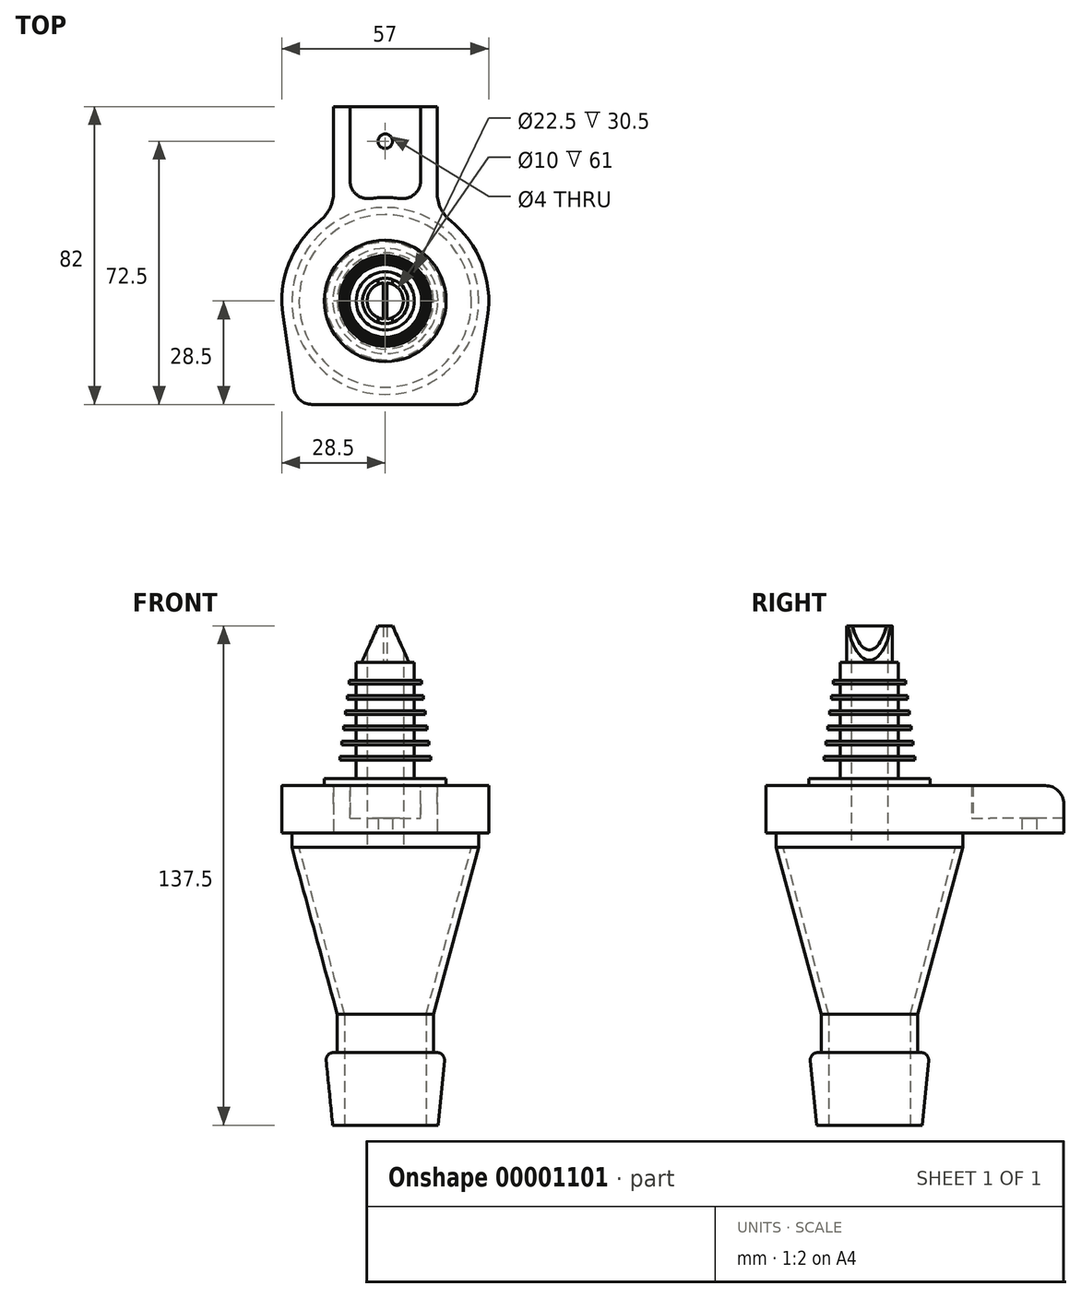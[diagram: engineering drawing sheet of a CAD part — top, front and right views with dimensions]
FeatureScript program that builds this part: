
annotation { "Feature Type Name" : "Feature", "Feature Type Description" : "" }
export const myFeature = defineFeature(function(context is Context, id is Id, definition is map)
    precondition{}
    {
        {
            var Q0;
            Q0=qCreatedBy(makeId("Right.planeOp"),FACE);
            var sketch = newSketch(context, id + "F0", { "sketchPlane" : qUnion([Q0])});
            skLineSegment(sketch, "E0", {"start": v(25.75, -4) * mm, "end": v(13.25, -50) * mm});
            skLineSegment(sketch, "E1", {"start": v(13.25, -50) * mm, "end": v(13.25, -60.5) * mm});
            skLineSegment(sketch, "E2", {"start": v(13.25, -60.5) * mm, "end": v(14.3, -60.5) * mm});
            skLineSegment(sketch, "E3", {"start": v(16.28, -62.7) * mm, "end": v(14.5, -80.5) * mm});
            skLineSegment(sketch, "E4", {"start": v(14.5, -80.5) * mm, "end": v(11.25, -80.5) * mm});
            skLineSegment(sketch, "E5", {"start": v(0, -80.5) * mm, "end": v(0, 57) * mm, "construction": true});
            skLineSegment(sketch, "E6", {"start": v(25.75, -4) * mm, "end": v(25.75, 0) * mm});
            skLineSegment(sketch, "E7", {"start": v(25.75, 0) * mm, "end": v(5, 0) * mm});
            skPoint(sketch, "E8.visualSharp", {"position": v(16.5, -60.5) * mm});
            skArc(sketch, "E8.filletArc", {"start": v(16.28, -62.7) * mm, "mid": v(15.77, -61.16) * mm, "end": v(14.3, -60.5) * mm});
            skLineSegment(sketch, "E9", {"start": v(11.25, -80.5) * mm, "end": v(11.25, -50) * mm});
            skLineSegment(sketch, "E10", {"start": v(13.25, -50) * mm, "end": v(11.25, -50) * mm});
            skLineSegment(sketch, "E11", {"start": v(11.25, -50) * mm, "end": v(23.75, -4) * mm});
            skLineSegment(sketch, "E12", {"start": v(23.75, -4) * mm, "end": v(5, -4) * mm});
            skLineSegment(sketch, "E13", {"start": v(0, -4) * mm, "end": v(0, 0) * mm});
            skLineSegment(sketch, "E14", {"start": v(5, 0) * mm, "end": v(5, -4) * mm});
            skLineSegment(sketch, "E15", {"start": v(16.75, 0) * mm, "end": v(16.75, 15) * mm});
            skLineSegment(sketch, "E16", {"start": v(16.75, 15) * mm, "end": v(13.5, 15) * mm});
            skLineSegment(sketch, "E17", {"start": v(13.5, 15) * mm, "end": v(13.5, 15) * mm});
            skLineSegment(sketch, "E18", {"start": v(13.5, 15) * mm, "end": v(8, 15) * mm});
            skLineSegment(sketch, "E19", {"start": v(8, 15) * mm, "end": v(8, 20) * mm});
            skLineSegment(sketch, "E20", {"start": v(8, 47) * mm, "end": v(6.25, 47) * mm});
            skLineSegment(sketch, "E21", {"start": v(6.25, 47) * mm, "end": v(6.25, 57) * mm});
            skLineSegment(sketch, "E22", {"start": v(6.25, 57) * mm, "end": v(5, 57) * mm});
            skLineSegment(sketch, "E23", {"start": v(5, 0) * mm, "end": v(5, 57) * mm});
            skLineSegment(sketch, "E24", {"start": v(8, 20) * mm, "end": v(12.5, 20) * mm});
            skLineSegment(sketch, "E25", {"start": v(12.5, 20) * mm, "end": v(12.5, 21) * mm});
            skLineSegment(sketch, "E26", {"start": v(12.5, 21) * mm, "end": v(8, 21) * mm});
            skLineSegment(sketch, "E27.0.1.0", {"start": v(12, 24.2) * mm, "end": v(12, 25.2) * mm});
            skLineSegment(sketch, "E27.0.1.1", {"start": v(12, 25.2) * mm, "end": v(8, 25.2) * mm});
            skLineSegment(sketch, "E27.0.1.2", {"start": v(8, 24.2) * mm, "end": v(12, 24.2) * mm});
            skLineSegment(sketch, "E27.0.2.0", {"start": v(11.5, 28.4) * mm, "end": v(11.5, 29.4) * mm});
            skLineSegment(sketch, "E27.0.2.1", {"start": v(11.5, 29.4) * mm, "end": v(8, 29.4) * mm});
            skLineSegment(sketch, "E27.0.2.2", {"start": v(8, 28.4) * mm, "end": v(11.5, 28.4) * mm});
            skLineSegment(sketch, "E27.0.3.0", {"start": v(11, 32.6) * mm, "end": v(11, 33.6) * mm});
            skLineSegment(sketch, "E27.0.3.1", {"start": v(11, 33.6) * mm, "end": v(8, 33.6) * mm});
            skLineSegment(sketch, "E27.0.3.2", {"start": v(8, 32.6) * mm, "end": v(11, 32.6) * mm});
            skLineSegment(sketch, "E27.0.4.0", {"start": v(10.5, 36.8) * mm, "end": v(10.5, 37.8) * mm});
            skLineSegment(sketch, "E27.0.4.1", {"start": v(10.5, 37.8) * mm, "end": v(8, 37.8) * mm});
            skLineSegment(sketch, "E27.0.4.2", {"start": v(8, 36.8) * mm, "end": v(10.5, 36.8) * mm});
            skLineSegment(sketch, "E27.0.5.0", {"start": v(10, 41) * mm, "end": v(10, 42) * mm});
            skLineSegment(sketch, "E27.0.5.1", {"start": v(10, 42) * mm, "end": v(8, 42) * mm});
            skLineSegment(sketch, "E27.0.5.2", {"start": v(8, 41) * mm, "end": v(10, 41) * mm});
            skLineSegment(sketch, "E28", {"start": v(12.5, 21) * mm, "end": v(10, 42) * mm, "construction": true});
            skLineSegment(sketch, "E29.trimOffspring", {"start": v(8, 42) * mm, "end": v(8, 47) * mm});
            skLineSegment(sketch, "E30.trimOffspring", {"start": v(8, 37.8) * mm, "end": v(8, 41) * mm});
            skLineSegment(sketch, "E31.trimOffspring", {"start": v(8, 33.6) * mm, "end": v(8, 36.8) * mm});
            skLineSegment(sketch, "E32.trimOffspring", {"start": v(8, 29.4) * mm, "end": v(8, 32.6) * mm});
            skLineSegment(sketch, "E33.trimOffspring", {"start": v(8, 25.2) * mm, "end": v(8, 28.4) * mm});
            skLineSegment(sketch, "E34.trimOffspring", {"start": v(8, 21) * mm, "end": v(8, 24.2) * mm});
            skSolve(sketch);
        }
        {
            var Q0;
            {var subQ0=sQuery(id+"F0.wireOp",EDGE,"E15");Q0=makeQuery(id+"F0.imprint","IMPRINT",FACE,{"disambiguationData":[TD([[makeQuery(id+"F0.imprint","IMPRINT",EDGE,{"derivedFrom":subQ0}),1.0]])]});}
            var Q1;
            Q1=makeQuery(id+"F0.imprint","IMPRINT",FACE,{"disambiguationData":[TD([[makeQuery(id+"F0.imprint","IMPRINT",EDGE,{"derivedFrom":sQuery(id+"F0.wireOp",EDGE,"E1")}),-1.0]])]});
            var Q2;
            Q2=sQuery(id+"F0.wireOp",EDGE,"E5");
            revolve(context, id + "F1", {"entities" : qUnion([Q0, Q1]), "axis" : qUnion([Q2]), "revolveType" : RevolveType.FULL});
        }
        {
            var Q0;
            Q0=makeQuery(id+"F0.imprint","IMPRINT",FACE,{"disambiguationData":[TD([[makeQuery(id+"F0.imprint","IMPRINT",EDGE,{"derivedFrom":sQuery(id+"F0.wireOp",EDGE,"E0")}),-1.0]])]});
            var Q1;
            Q1=sQuery(id+"F0.wireOp",EDGE,"E5");
            revolve(context, id + "F2", {"entities" : qUnion([Q0]), "axis" : qUnion([Q1]), "revolveType" : RevolveType.FULL});
        }
        {
            var Q0;
            Q0=qCreatedBy(makeId("Front.planeOp"),FACE);
            var sketch = newSketch(context, id + "F3", { "sketchPlane" : qUnion([Q0])});
            skLineSegment(sketch, "E35.bottom", {"start": v(0.5, 57) * mm, "end": v(-0.5, 57) * mm});
            skLineSegment(sketch, "E35.top", {"start": v(0.5, 47) * mm, "end": v(-0.5, 47) * mm});
            skLineSegment(sketch, "E35.left", {"start": v(0.5, 57) * mm, "end": v(0.5, 47) * mm});
            skLineSegment(sketch, "E35.right", {"start": v(-0.5, 57) * mm, "end": v(-0.5, 47) * mm});
            skPoint(sketch, "E35.middle", {"position": v(0, 52) * mm});
            skLineSegment(sketch, "E36", {"start": v(2, 57) * mm, "end": v(6.5, 47) * mm});
            skLineSegment(sketch, "E37", {"start": v(-6.5, 47) * mm, "end": v(-2, 57) * mm});
            skLineSegment(sketch, "E38", {"start": v(0, 57) * mm, "end": v(0, 47) * mm, "construction": true});
            skLineSegment(sketch, "E39.bottom", {"start": v(6.5, 47) * mm, "end": v(-6.5, 47) * mm});
            skLineSegment(sketch, "E39.top", {"start": v(6.5, 57) * mm, "end": v(-6.5, 57) * mm});
            skLineSegment(sketch, "E39.left", {"start": v(6.5, 47) * mm, "end": v(6.5, 57) * mm});
            skLineSegment(sketch, "E39.right", {"start": v(-6.5, 47) * mm, "end": v(-6.5, 57) * mm});
            skSolve(sketch);
        }
        {
            var Q0;
            {var subQ0=sQuery(id+"F3.wireOp",EDGE,"E37");Q0=makeQuery(id+"F3.imprint","IMPRINT",FACE,{"disambiguationData":[TD([[makeQuery(id+"F3.imprint","IMPRINT",EDGE,{"derivedFrom":subQ0}),1.0]])]});}
            var Q1;
            {var subQ0=sQuery(id+"F3.wireOp",EDGE,"E36");Q1=makeQuery(id+"F3.imprint","IMPRINT",FACE,{"disambiguationData":[TD([[makeQuery(id+"F3.imprint","IMPRINT",EDGE,{"derivedFrom":subQ0}),1.0]])]});}
            extrude(context, id + "F4", {"entities" : qUnion([Q0, Q1]), "operationType" : NewBodyOperationType.REMOVE, "oppositeDirection" : true, "depth" : 25 * mm, "symmetric" : true});
        }
        {
            var Q0;
            {var subQ0=sQuery(id+"F3.wireOp",EDGE,"E35.left");Q0=makeQuery(id+"F3.imprint","IMPRINT",FACE,{"disambiguationData":[TD([[makeQuery(id+"F3.imprint","IMPRINT",EDGE,{"derivedFrom":subQ0}),-1.0]])]});}
            extrude(context, id + "F5", {"entities" : qUnion([Q0]), "operationType" : NewBodyOperationType.ADD, "depth" : 11 * mm, "symmetric" : true});
        }
        {
            var Q0;
            Q0=makeQuery(id+"F2.opRevolve","SWEPT_FACE",FACE,{"disambiguationData":[OSD([sQuery(id+"F0.wireOp",EDGE,"E7")])]});
            var sketch = newSketch(context, id + "F6", { "sketchPlane" : qUnion([Q0])});
            skLineSegment(sketch, "E40", {"start": v(-24.5, -28.5) * mm, "end": v(24.5, -28.5) * mm});
            skLineSegment(sketch, "E41", {"start": v(24.5, -28.5) * mm, "end": v(28.18, -4.28) * mm});
            skArc(sketch, "E42", {"start": v(28.18, -4.28) * mm, "mid": v(26.58, 10.29) * mm, "end": v(17.95, 22.14) * mm});
            skLineSegment(sketch, "E43", {"start": v(-24.5, -28.5) * mm, "end": v(-28.18, -4.28) * mm});
            skLineSegment(sketch, "E44", {"start": v(28.18, -4.28) * mm, "end": v(-28.18, -4.28) * mm, "construction": true});
            skLineSegment(sketch, "E45.bottom", {"start": v(-14.25, 53.5) * mm, "end": v(14.25, 53.5) * mm});
            skLineSegment(sketch, "E45.left", {"start": v(-14.25, 53.5) * mm, "end": v(-14.25, 29.9) * mm});
            skLineSegment(sketch, "E45.right", {"start": v(14.25, 53.5) * mm, "end": v(14.25, 29.9) * mm});
            skArc(sketch, "E46.filletArc", {"start": v(14.25, 29.9) * mm, "mid": v(15.22, 25.6) * mm, "end": v(17.95, 22.14) * mm});
            skArc(sketch, "E47.MirrorCS", {"start": v(-28.18, -4.28) * mm, "mid": v(-26.58, 10.29) * mm, "end": v(-17.95, 22.14) * mm});
            skArc(sketch, "E48.MirrorCS", {"start": v(-14.25, 29.9) * mm, "mid": v(-15.22, 25.6) * mm, "end": v(-17.95, 22.14) * mm});
            skCircle(sketch, "E49", {"center": v(0, 44) * mm, "radius": 2 * mm});
            skLineSegment(sketch, "E50", {"start": v(9.75, 53.5) * mm, "end": v(9.75, 26.78) * mm});
            skLineSegment(sketch, "E51", {"start": v(-9.75, 26.78) * mm, "end": v(-9.75, 53.5) * mm});
            skLineSegment(sketch, "E52", {"start": v(0, 0) * mm, "end": v(0, 44) * mm, "construction": true});
            skArc(sketch, "E53", {"start": v(9.75, 26.78) * mm, "mid": v(0, 28.5) * mm, "end": v(-9.75, 26.78) * mm});
            skCircle(sketch, "E54", {"center": v(0, 0) * mm, "radius": 5 * mm});
            skSolve(sketch);
        }
        {
            var Q0;
            Q0=makeQuery(id+"F6.imprint","IMPRINT",FACE,{"disambiguationData":[TD([[makeQuery(id+"F6.imprint","IMPRINT",EDGE,{"derivedFrom":makeQuery(id+"F2.opRevolve","SWEPT_EDGE",EDGE,{"disambiguationData":[OSD([sQuery(id+"F0.wireOp",EDGE,"E7"),sQuery(id+"F0.wireOp",EDGE,"E14"),sQuery(id+"F0.wireOp",EDGE,"E23")])]})}),-1.0]])]});
            var Q1;
            Q1=makeQuery(id+"F6.imprint","IMPRINT",FACE,{"disambiguationData":[TD([[makeQuery(id+"F6.imprint","IMPRINT",EDGE,{"derivedFrom":sQuery(id+"F6.wireOp",EDGE,"E40")}),1.0]])]});
            var Q2;
            {var subQ0=sQuery(id+"F0.wireOp",EDGE,"E7");Q2=makeQuery(id+"F6.imprint","IMPRINT",FACE,{"disambiguationData":[TD([[makeQuery(id+"F6.imprint","IMPRINT",EDGE,{"derivedFrom":makeQuery(id+"F2.opRevolve","SWEPT_EDGE",EDGE,{"disambiguationData":[OSD([sQuery(id+"F0.wireOp",EDGE,"E6"),subQ0])]})}),-1.0]])]});}
            extrude(context, id + "F7", {"entities" : qUnion([Q0, Q1, Q2]), "operationType" : NewBodyOperationType.ADD, "depth" : 13 * mm});
        }
        {
            var Q0;
            Q0=makeQuery(id+"F6.imprint","IMPRINT",FACE,{"disambiguationData":[TD([[makeQuery(id+"F6.imprint","IMPRINT",EDGE,{"derivedFrom":sQuery(id+"F6.wireOp",EDGE,"E49")}),-1.0]])]});
            extrude(context, id + "F8", {"entities" : qUnion([Q0]), "operationType" : NewBodyOperationType.ADD, "depth" : 4 * mm});
        }
        {
            var Q0;
            {var subQ0=sQuery(id+"F6.wireOp",EDGE,"E45.bottom");Q0=makeQuery(id+"F7.opExtrude","CAP_EDGE",EDGE,{"disambiguationData":[OSD([subQ0]),TDD([makeQuery(id+"F6.imprint","IMPRINT",EDGE,{"disambiguationData":[TD([[makeQuery(id+"F6.imprint","INTERSECT",VERTEX,{"derivedFrom":[subQ0,sQuery(id+"F6.wireOp",EDGE,"E45.right")]}),1.0]])],"derivedFrom":subQ0})])],"isStart":false});}
            var Q1;
            {var subQ0=sQuery(id+"F6.wireOp",EDGE,"E45.bottom");Q1=makeQuery(id+"F7.opExtrude","CAP_EDGE",EDGE,{"disambiguationData":[OSD([subQ0]),TDD([makeQuery(id+"F6.imprint","IMPRINT",EDGE,{"disambiguationData":[TD([[makeQuery(id+"F6.imprint","INTERSECT",VERTEX,{"derivedFrom":[subQ0,sQuery(id+"F6.wireOp",EDGE,"E45.left")]}),-1.0]])],"derivedFrom":subQ0})])],"isStart":false});}
            var Q2;
            Q2=makeQuery(id+"F7.opExtrude","SWEPT_EDGE",EDGE,{"disambiguationData":[OSD([sQuery(id+"F6.wireOp",EDGE,"E40"),sQuery(id+"F6.wireOp",EDGE,"E41")])]});
            var Q3;
            Q3=makeQuery(id+"F7.opExtrude","SWEPT_EDGE",EDGE,{"disambiguationData":[OSD([sQuery(id+"F6.wireOp",EDGE,"E40"),sQuery(id+"F6.wireOp",EDGE,"E43")])]});
            var Q4;
            Q4=makeQuery(id+"F7.opExtrude","SWEPT_EDGE",EDGE,{"disambiguationData":[OSD([sQuery(id+"F6.wireOp",EDGE,"E51"),sQuery(id+"F6.wireOp",EDGE,"E53")])]});
            var Q5;
            Q5=makeQuery(id+"F7.opExtrude","SWEPT_EDGE",EDGE,{"disambiguationData":[OSD([sQuery(id+"F6.wireOp",EDGE,"E50"),sQuery(id+"F6.wireOp",EDGE,"E53")])]});
            fillet(context, id + "F9", {"entities" : qUnion([Q0, Q1, Q2, Q3, Q4, Q5]), "radius" : 5 * mm, "tangentPropagation" : true, "allowEdgeOverflow" : false});
        }
        {
            var Q0;
            Q0=qCreatedBy(makeId("Right.planeOp"),FACE);
            var sketch = newSketch(context, id + "F10", { "sketchPlane" : qUnion([Q0])});
            skArc(sketch, "E55", {"start": v(-19.2, -62.55) * mm, "mid": v(-31.2, -77.12) * mm, "end": v(-35.5, -95.5) * mm});
            skLineSegment(sketch, "E56", {"start": v(-16.25, -60.5) * mm, "end": v(-13.25, -60.5) * mm});
            skCircle(sketch, "E57", {"center": v(-28, -89.5) * mm, "radius": 2.5 * mm});
            skLineSegment(sketch, "E58", {"start": v(14.5, -95.5) * mm, "end": v(14.5, -80.5) * mm, "construction": true});
            skLineSegment(sketch, "E59", {"start": v(16.5, -60.5) * mm, "end": v(-16.25, -60.5) * mm});
            skLineSegment(sketch, "E60", {"start": v(-23.5, -95.5) * mm, "end": v(-35.5, -95.5) * mm});
            skLineSegment(sketch, "E61", {"start": v(-13.13, -60.5) * mm, "end": v(16.5, -60.5) * mm});
            skLineSegment(sketch, "E62", {"start": v(-35.5, -95.5) * mm, "end": v(14.5, -95.5) * mm, "construction": true});
            skLineSegment(sketch, "E63", {"start": v(16.5, -63.5) * mm, "end": v(16.5, -60.5) * mm});
            skArc(sketch, "E64", {"start": v(16.5, -63.5) * mm, "mid": v(-11.19, -69.89) * mm, "end": v(-23.5, -95.5) * mm});
            skPoint(sketch, "E65.visualSharp", {"position": v(-16.25, -60.5) * mm});
            skArc(sketch, "E65.filletArc", {"start": v(-13.13, -60.5) * mm, "mid": v(-16.33, -61.03) * mm, "end": v(-19.2, -62.55) * mm});
            skSolve(sketch);
        }
    });
